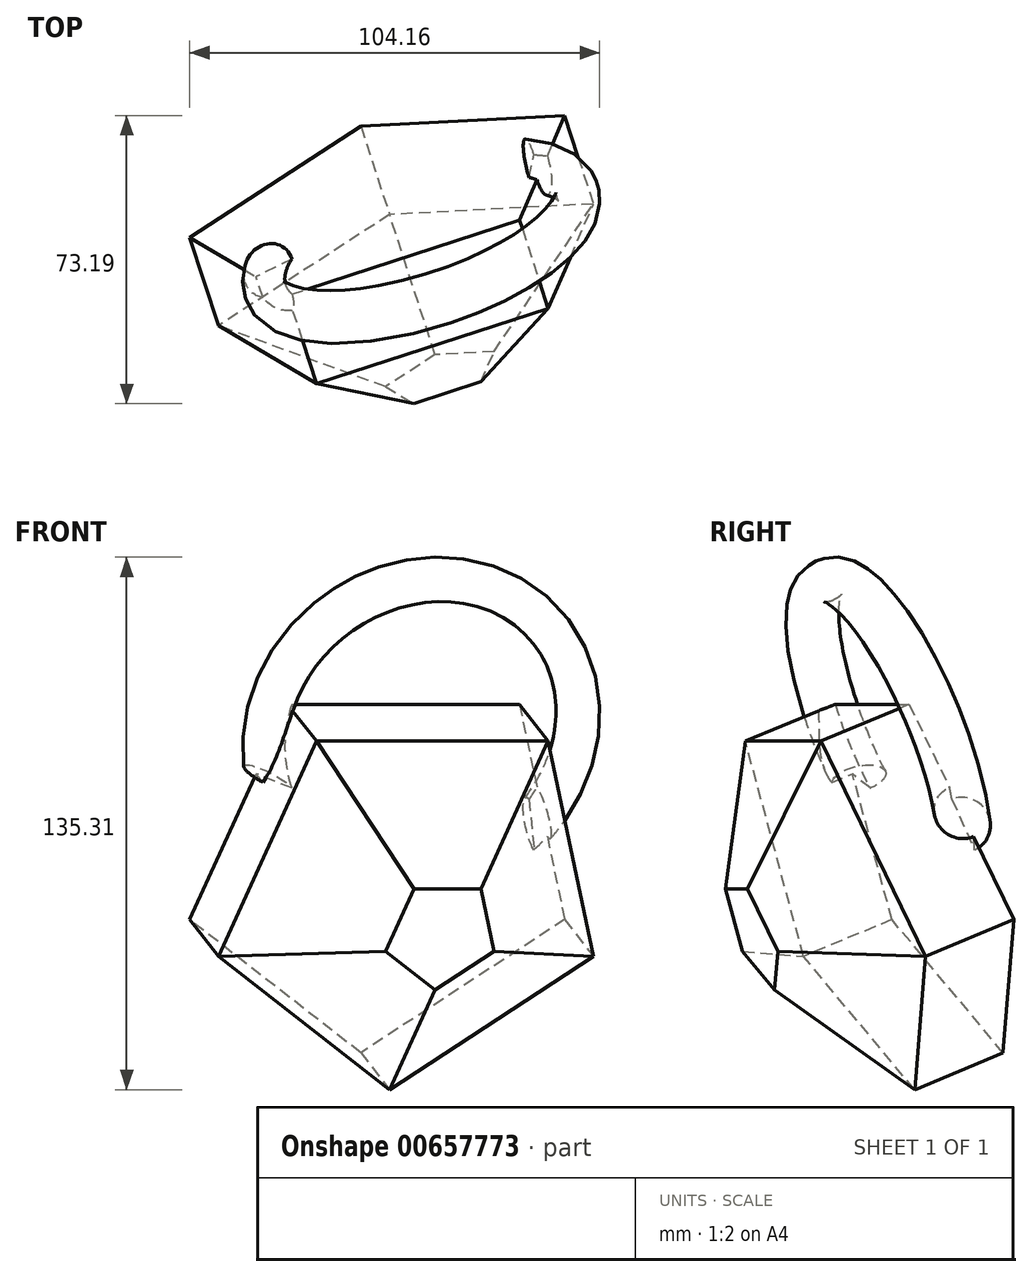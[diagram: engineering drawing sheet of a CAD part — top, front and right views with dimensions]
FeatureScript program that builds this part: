
annotation { "Feature Type Name" : "Feature", "Feature Type Description" : "" }
export const myFeature = defineFeature(function(context is Context, id is Id, definition is map)
    precondition{}
    {
        {
            var Q0;
            Q0=qCreatedBy(makeId("Top.planeOp"),FACE);
            var sketch = newSketch(context, id + "F0", { "sketchPlane" : qUnion([Q0])});
            skCircle(sketch, "E0.cCircle", {"center": v(0, 0) * mm, "radius": 42.6 * mm, "construction": true});
            skLineSegment(sketch, "E0.0", {"start": v(42.6, 30.95) * mm, "end": v(42.6, -30.95) * mm});
            skLineSegment(sketch, "E0.1", {"start": v(42.6, -30.95) * mm, "end": v(-16.27, -50.09) * mm});
            skLineSegment(sketch, "E0.2", {"start": v(-16.27, -50.09) * mm, "end": v(-52.66, 0) * mm});
            skLineSegment(sketch, "E0.3", {"start": v(-52.66, 0) * mm, "end": v(-16.27, 50.09) * mm});
            skLineSegment(sketch, "E0.4", {"start": v(-16.27, 50.09) * mm, "end": v(42.6, 30.95) * mm});
            skPoint(sketch, "E0.0.midPoint", {"position": v(42.6, 0) * mm});
            skSolve(sketch);
        }
        {
            var Q0;
            Q0 = qSketchRegion(id + "F0", true);
            extrude(context, id + "F1", {"entities" : qUnion([Q0]), "depth" : 25.4 * mm, "offsetDistance" : 25.4 * mm, "hasDraft" : true, "draftAngle" : 50 * degree, "draftPullDirection" : true});
        }
        {
            var Q0;
            Q0=makeQuery(id+"F1.opExtrude","CAP_FACE",FACE,{"disambiguationData":[OSD([sQuery(id+"F0.wireOp",EDGE,"E0.0"),sQuery(id+"F0.wireOp",EDGE,"E0.1"),sQuery(id+"F0.wireOp",EDGE,"E0.2"),sQuery(id+"F0.wireOp",EDGE,"E0.3"),sQuery(id+"F0.wireOp",EDGE,"E0.4")])],"isStart":true});
            var sketch = newSketch(context, id + "F2", { "sketchPlane" : qUnion([Q0])});
            skSolve(sketch);
        }
        {
            var Q0;
            Q0=makeQuery(id+"F2.imprint","IMPRINT",FACE,{"disambiguationData":[TD([[makeQuery(id+"F2.imprint","IMPRINT",EDGE,{"derivedFrom":makeQuery(id+"F1.opExtrude","CAP_EDGE",EDGE,{"disambiguationData":[OSD([sQuery(id+"F0.wireOp",EDGE,"E0.0")])],"isStart":true})}),1.0]])]});
            extrude(context, id + "F3", {"entities" : qUnion([Q0]), "operationType" : NewBodyOperationType.ADD, "depth" : 25.4 * mm, "offsetDistance" : 25.4 * mm});
        }
        {
            var Q0;
            Q0=makeQuery(id+"F3.opExtrude","CAP_FACE",FACE,{"disambiguationData":[OSD([sQuery(id+"F0.wireOp",EDGE,"E0.0"),sQuery(id+"F0.wireOp",EDGE,"E0.1"),sQuery(id+"F0.wireOp",EDGE,"E0.2"),sQuery(id+"F0.wireOp",EDGE,"E0.3"),sQuery(id+"F0.wireOp",EDGE,"E0.4")])],"isStart":false});
            cPlane(context, id + "F4", {"entities" : qUnion([Q0]), "cplaneType" : CPlaneType.OFFSET, "offset" : 5.08 * mm, "oppositeDirection" : true, "width" : 152.4 * mm, "height" : 152.4 * mm});
        }
        {
            var Q0;
            Q0=qCreatedBy(id+"F4.planeOp",FACE);
            var sketch = newSketch(context, id + "F5", { "sketchPlane" : qUnion([Q0])});
            skArc(sketch, "E1", {"start": v(39.55, 10.8) * mm, "mid": v(11.07, 76.7) * mm, "end": v(-33.57, 20.47) * mm});
            skSolve(sketch);
        }
        {
            var Q0;
            Q0=makeQuery(id+"F3.opExtrude","SWEPT_FACE",FACE,{"disambiguationData":[OSD([sQuery(id+"F0.wireOp",EDGE,"E0.2")])]});
            var sketch = newSketch(context, id + "F6", { "sketchPlane" : qUnion([Q0])});
            skCircle(sketch, "E2", {"center": v(0, -25.4) * mm, "radius": 7.06 * mm});
            skSolve(sketch);
        }
        {
            var Q0;
            {var subQ0=sQuery(id+"F6.wireOp",EDGE,"E2");var subQ1=makeQuery(id+"F3.opExtrude","CAP_EDGE",EDGE,{"disambiguationData":[OSD([sQuery(id+"F0.wireOp",EDGE,"E0.2")])],"isStart":false});var subQ2=makeQuery(id+"F6.imprint","INTERSECT",VERTEX,{"disambiguationData":[OD(0.0)],"derivedFrom":[subQ1,subQ0]});Q0=makeQuery(id+"F6.imprint","IMPRINT",FACE,{"disambiguationData":[TD([[makeQuery(id+"F6.imprint","IMPRINT",EDGE,{"disambiguationData":[TD([[subQ2,1.0]])],"derivedFrom":subQ0}),1.0]])]});}
            var Q1;
            {var subQ0=sQuery(id+"F6.wireOp",EDGE,"E2");var subQ1=makeQuery(id+"F3.opExtrude","CAP_EDGE",EDGE,{"disambiguationData":[OSD([sQuery(id+"F0.wireOp",EDGE,"E0.2")])],"isStart":false});var subQ2=makeQuery(id+"F6.imprint","INTERSECT",VERTEX,{"disambiguationData":[OD(0.0)],"derivedFrom":[subQ1,subQ0]});Q1=makeQuery(id+"F6.imprint","IMPRINT",FACE,{"disambiguationData":[TD([[makeQuery(id+"F6.imprint","IMPRINT",EDGE,{"disambiguationData":[TD([[subQ2,-1.0]])],"derivedFrom":subQ0}),1.0]])]});}
            var Q2;
            Q2=sQuery(id+"F5.wireOp",EDGE,"E1");
            sweep(context, id + "F7", {"operationType" : NewBodyOperationType.ADD, "profiles" : qUnion([Q0, Q1]), "path" : qUnion([Q2])});
        }
        {
            var Q0;
            Q0=makeQuery(id+"F1.opExtrude","SWEPT_BODY",BODY,{"disambiguationData":[OSD([sQuery(id+"F0.wireOp",EDGE,"E0.0"),sQuery(id+"F0.wireOp",EDGE,"E0.1"),sQuery(id+"F0.wireOp",EDGE,"E0.2"),sQuery(id+"F0.wireOp",EDGE,"E0.3"),sQuery(id+"F0.wireOp",EDGE,"E0.4")])]});
            var Q1;
            Q1=makeQuery(id+"F1.opExtrude","SWEPT_EDGE",EDGE,{"disambiguationData":[OSD([sQuery(id+"F0.wireOp",EDGE,"E0.3"),sQuery(id+"F0.wireOp",EDGE,"E0.4")])]});
            transform(context, id + "F8", {"entities" : qUnion([Q0]), "transformType" : TransformType.ROTATION, "transformAxis" : qUnion([Q1]), "angle" : 180 * degree, "makeCopy" : false});
        }
    });
